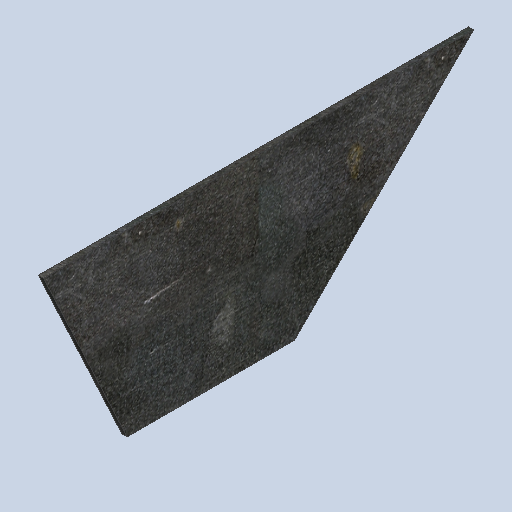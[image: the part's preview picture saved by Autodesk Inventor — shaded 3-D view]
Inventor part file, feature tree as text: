
AUTODESK INVENTOR PART (.ipt)
format: ipt  version: 2024.3 (Build 283343000, 343)  size: 220,672 bytes
history: native  units: mm
features: extrude x1, sketch x1
ambient origin geometry x8: Origin, YZ Plane, XZ Plane, XY Plane, X Axis, Y Axis, Z Axis, Center Point
bodies: Solid1 (feature_tree)
feature tree (2):
  extrude  "Extrusion1"  Depth=114.554mm
  sketch  "Sketch1"  dims[d0=97.0mm d1=114.554mm d2=45.0deg d3=4.363323mm d4=3.0mm d5=0.0mm]
